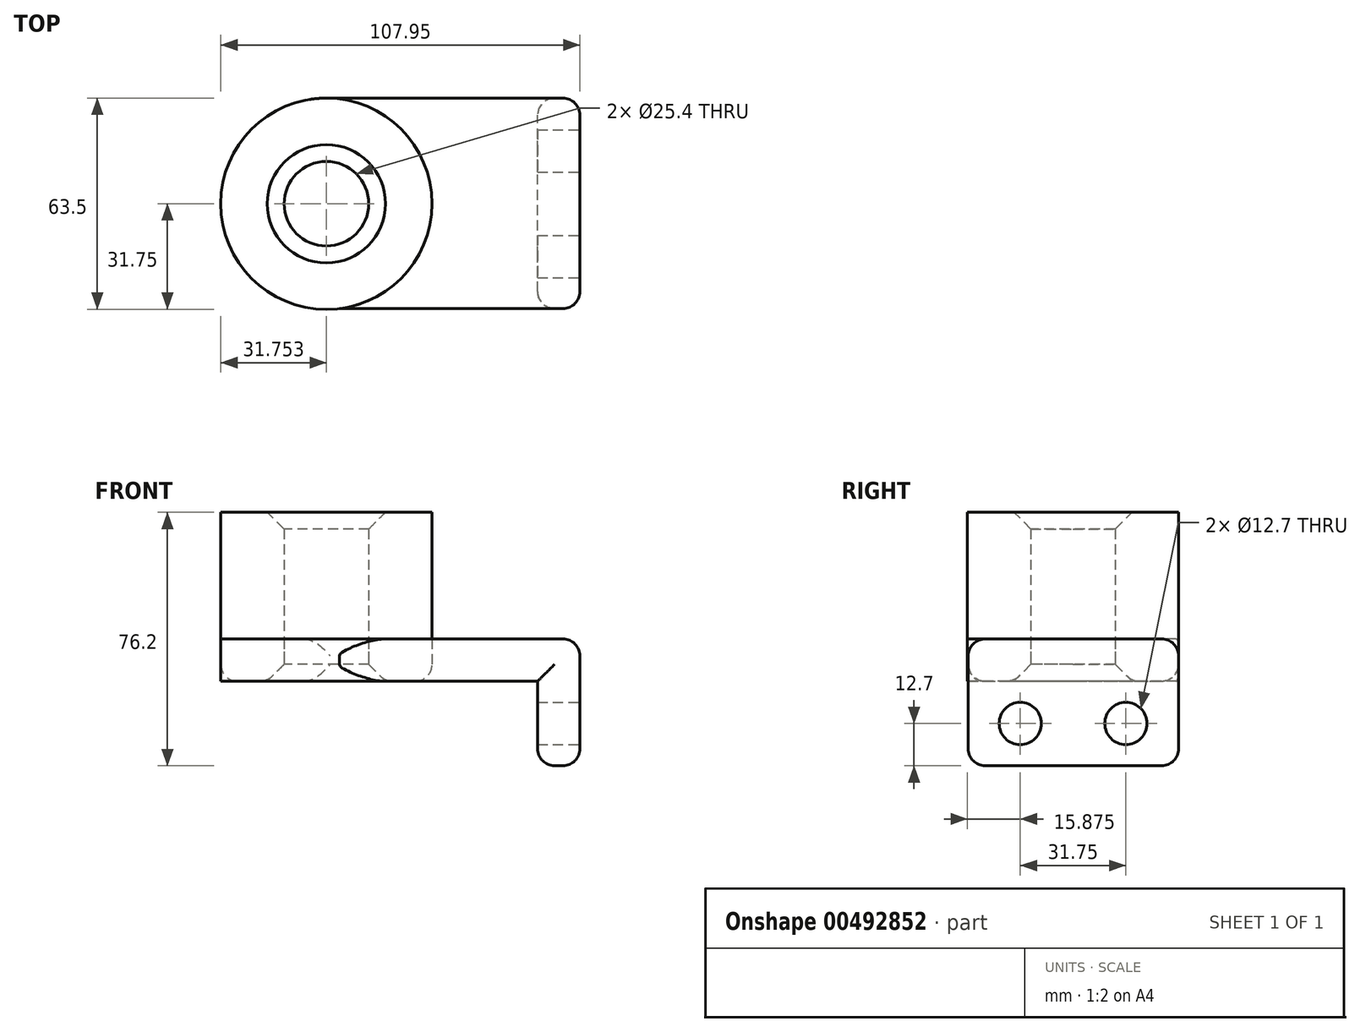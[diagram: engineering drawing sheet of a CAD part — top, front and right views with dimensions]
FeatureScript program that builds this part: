
annotation { "Feature Type Name" : "Feature", "Feature Type Description" : "" }
export const myFeature = defineFeature(function(context is Context, id is Id, definition is map)
    precondition{}
    {
        {
            var Q0;
            Q0=qCreatedBy(makeId("Top.planeOp"),FACE);
            var sketch = newSketch(context, id + "F0", { "sketchPlane" : qUnion([Q0])});
            skLineSegment(sketch, "E0.bottom", {"start": v(-42.95, 31.72) * mm, "end": v(33.25, 31.72) * mm});
            skLineSegment(sketch, "E0.top", {"start": v(-42.95, -31.5) * mm, "end": v(33.25, -31.5) * mm});
            skLineSegment(sketch, "E0.left", {"start": v(-42.95, 31.72) * mm, "end": v(-42.95, -31.5) * mm});
            skLineSegment(sketch, "E0.right", {"start": v(33.25, 31.72) * mm, "end": v(33.25, -31.5) * mm});
            skCircle(sketch, "E1", {"center": v(-42.95, 0) * mm, "radius": 31.75 * mm});
            skCircle(sketch, "E2", {"center": v(-42.95, 0) * mm, "radius": 12.7 * mm});
            skSolve(sketch);
        }
        {
            var Q0;
            Q0 = qSketchRegion(id + "F0", true);
            extrude(context, id + "F1", {"entities" : qUnion([Q0]), "depth" : 12.7 * mm});
        }
        {
            var Q0;
            {var subQ0=sQuery(id+"F0.wireOp",EDGE,"E0.left");var subQ5=sQuery(id+"F0.wireOp",EDGE,"E0.bottom");var subQ6=makeQuery(id+"F0.imprint","INTERSECT",VERTEX,{"derivedFrom":[subQ5,subQ0]});Q0=makeQuery(id+"F0.imprint","IMPRINT",FACE,{"disambiguationData":[TD([[makeQuery(id+"F0.imprint","IMPRINT",EDGE,{"disambiguationData":[TD([[subQ6,-1.0]])],"derivedFrom":subQ5}),-1.0]])]});}
            var Q1;
            {var subQ0=sQuery(id+"F0.wireOp",EDGE,"E0.left");var subQ5=sQuery(id+"F0.wireOp",EDGE,"E0.bottom");var subQ6=makeQuery(id+"F0.imprint","INTERSECT",VERTEX,{"derivedFrom":[subQ5,subQ0]});Q1=makeQuery(id+"F0.imprint","IMPRINT",FACE,{"disambiguationData":[TD([[makeQuery(id+"F0.imprint","IMPRINT",EDGE,{"disambiguationData":[TD([[subQ6,-1.0]])],"derivedFrom":subQ5}),1.0]])]});}
            var Q2;
            Q2=sQuery(id+"F0.wireOp",EDGE,"E2");
            var Q3;
            Q3=sQuery(id+"F0.wireOp",EDGE,"E1");
            extrude(context, id + "F2", {"entities" : qUnion([Q0, Q1]), "surfaceEntities" : qUnion([Q2, Q3]), "depth" : 50.8 * mm});
        }
        {
            var Q0;
            Q0=makeQuery(id+"F1.opExtrude","SWEPT_FACE",FACE,{"disambiguationData":[OSD([sQuery(id+"F0.wireOp",EDGE,"E0.right")])]});
            var sketch = newSketch(context, id + "F3", { "sketchPlane" : qUnion([Q0])});
            skLineSegment(sketch, "E3.bottom", {"start": v(-31.5, 12.7) * mm, "end": v(31.72, 12.7) * mm});
            skLineSegment(sketch, "E3.top", {"start": v(-31.5, -25.4) * mm, "end": v(31.72, -25.4) * mm});
            skLineSegment(sketch, "E3.left", {"start": v(-31.5, 12.7) * mm, "end": v(-31.5, -25.4) * mm});
            skLineSegment(sketch, "E3.right", {"start": v(31.72, 12.7) * mm, "end": v(31.72, -25.4) * mm});
            skLineSegment(sketch, "E4", {"start": v(0, 0) * mm, "end": v(0, -25.4) * mm});
            skCircle(sketch, "E5", {"center": v(-15.87, -12.7) * mm, "radius": 6.35 * mm});
            skCircle(sketch, "E6.MirrorC", {"center": v(15.88, -12.7) * mm, "radius": 6.35 * mm});
            skSolve(sketch);
        }
        {
            var Q0;
            Q0 = qSketchRegion(id + "F3", true);
            extrude(context, id + "F4", {"entities" : qUnion([Q0]), "operationType" : NewBodyOperationType.ADD, "oppositeDirection" : true, "depth" : 12.7 * mm});
        }
        {
            var Q0;
            Q0=makeQuery(id+"F1.opExtrude","CAP_EDGE",EDGE,{"disambiguationData":[OSD([sQuery(id+"F0.wireOp",EDGE,"E0.right")])],"isStart":false});
            var Q1;
            Q1=makeQuery(id+"F4.opExtrude","SWEPT_EDGE",EDGE,{"disambiguationData":[OSD([sQuery(id+"F3.wireOp",EDGE,"E3.top"),sQuery(id+"F3.wireOp",EDGE,"E3.left")])]});
            var Q2;
            Q2=makeQuery(id+"F4.opExtrude","SWEPT_EDGE",EDGE,{"disambiguationData":[OSD([sQuery(id+"F3.wireOp",EDGE,"E3.top"),sQuery(id+"F3.wireOp",EDGE,"E3.right")])]});
            fillet(context, id + "F5", {"entities" : qUnion([Q0, Q1, Q2]), "radius" : 5.08 * mm, "tangentPropagation" : true, "allowEdgeOverflow" : false});
        }
        {
            var Q0;
            Q0=makeQuery(id+"F2.opExtrude","CAP_EDGE",EDGE,{"disambiguationData":[OSD([sQuery(id+"F0.wireOp",EDGE,"E2")])],"isStart":true});
            var Q1;
            Q1=makeQuery(id+"F1.opExtrude","CAP_EDGE",EDGE,{"disambiguationData":[OSD([sQuery(id+"F0.wireOp",EDGE,"E2")])],"isStart":true});
            var Q2;
            Q2=makeQuery(id+"F2.opExtrude","CAP_EDGE",EDGE,{"disambiguationData":[OSD([sQuery(id+"F0.wireOp",EDGE,"E2")])],"isStart":false});
            chamfer(context, id + "F6", {"entities" : qUnion([Q0, Q1, Q2]), "width" : 5.08 * mm, "tangentPropagation" : true});
        }
        {
            var Q0;
            Q0=makeQuery(id+"F1.opExtrude","CAP_EDGE",EDGE,{"disambiguationData":[OSD([sQuery(id+"F0.wireOp",EDGE,"E0.top")])],"isStart":false});
            var Q1;
            Q1=makeQuery(id+"F1.opExtrude","CAP_EDGE",EDGE,{"disambiguationData":[OSD([sQuery(id+"F0.wireOp",EDGE,"E0.top")])],"isStart":true});
            var Q2;
            Q2=makeQuery(id+"F4.boolean.opBoolean","MERGE",FACE,{"derivedFrom":[makeQuery(id+"F1.opExtrude","SWEPT_FACE",FACE,{"disambiguationData":[OSD([sQuery(id+"F0.wireOp",EDGE,"E0.bottom")])]}),makeQuery(id+"F4.opExtrude","SWEPT_FACE",FACE,{"disambiguationData":[OSD([sQuery(id+"F3.wireOp",EDGE,"E3.right")])]})]});
            var Q3;
            Q3=makeQuery(id+"F1.opExtrude","CAP_EDGE",EDGE,{"disambiguationData":[OSD([sQuery(id+"F0.wireOp",EDGE,"E0.bottom")])],"isStart":true});
            var Q4;
            Q4=makeQuery(id+"F1.opExtrude","CAP_EDGE",EDGE,{"disambiguationData":[OSD([sQuery(id+"F0.wireOp",EDGE,"E0.bottom")])],"isStart":false});
            var Q5;
            Q5=makeQuery(id+"F2.opExtrude","CAP_FACE",FACE,{"disambiguationData":[OSD([sQuery(id+"F0.wireOp",EDGE,"E1"),sQuery(id+"F0.wireOp",EDGE,"E2")])],"isStart":true});
            fillet(context, id + "F7", {"entities" : qUnion([Q0, Q1, Q2, Q3, Q4, Q5]), "radius" : 5.08 * mm, "tangentPropagation" : true, "allowEdgeOverflow" : false});
        }
    });
